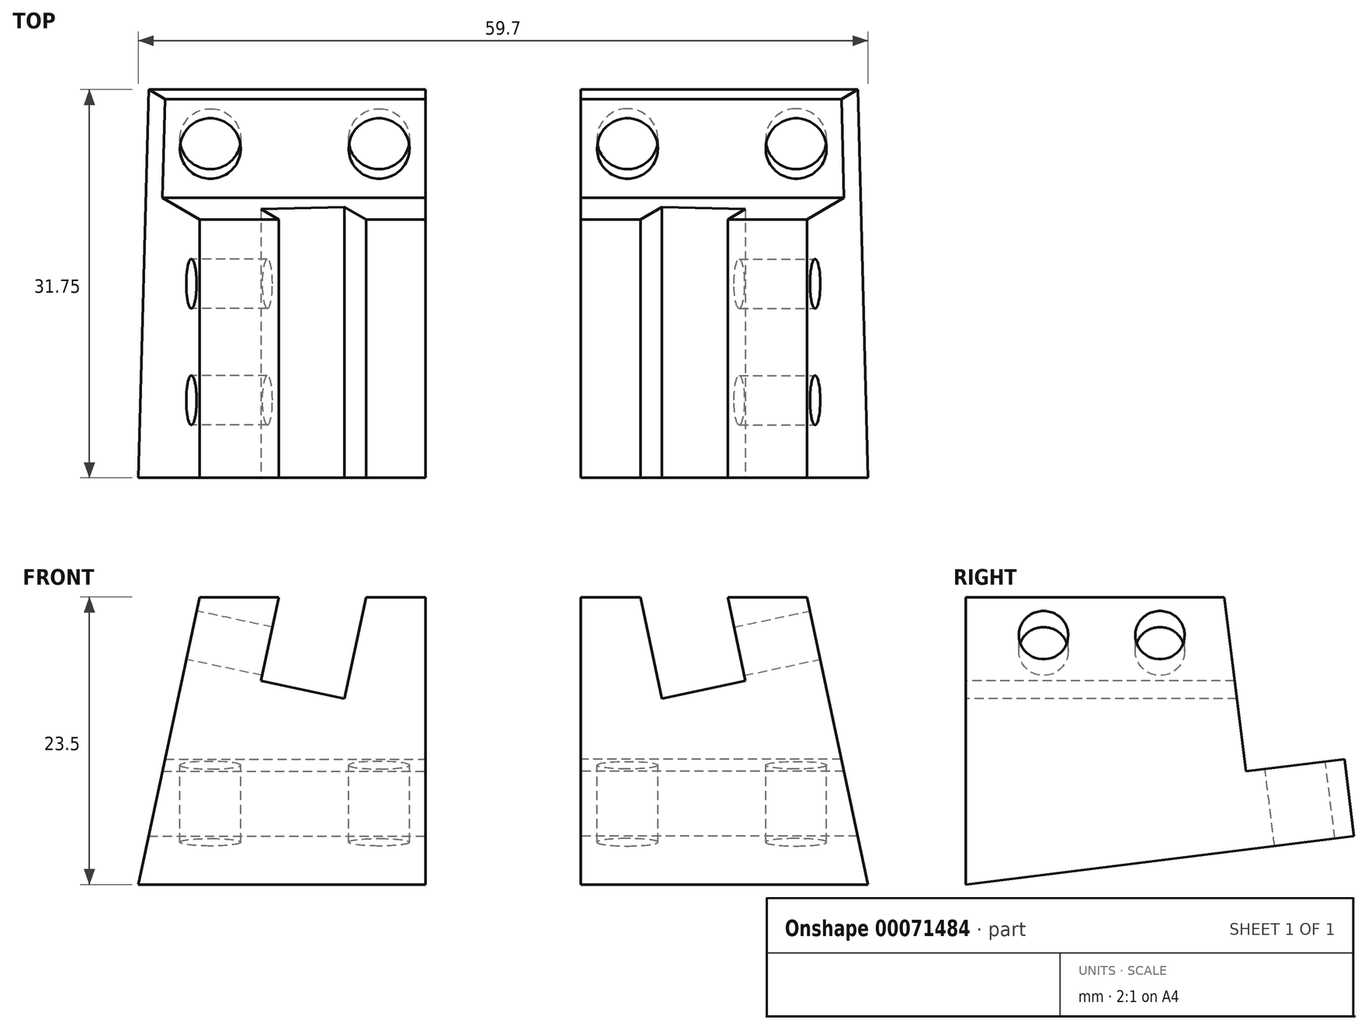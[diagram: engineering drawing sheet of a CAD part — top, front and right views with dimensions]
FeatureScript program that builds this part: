
annotation { "Feature Type Name" : "Feature", "Feature Type Description" : "" }
export const myFeature = defineFeature(function(context is Context, id is Id, definition is map)
    precondition{}
    {
        {
            var Q0;
            Q0=qCreatedBy(makeId("Front.planeOp"),FACE);
            var sketch = newSketch(context, id + "F0", { "sketchPlane" : qUnion([Q0])});
            skLineSegment(sketch, "E0.bottom", {"start": v(-29.85, 0) * mm, "end": v(-6.35, 0) * mm});
            skLineSegment(sketch, "E0.top", {"start": v(-29.85, 23.5) * mm, "end": v(-6.35, 23.5) * mm});
            skLineSegment(sketch, "E0.left", {"start": v(-29.85, 0) * mm, "end": v(-29.85, 23.5) * mm});
            skLineSegment(sketch, "E0.right", {"start": v(-6.35, 0) * mm, "end": v(-6.35, 23.5) * mm});
            skSolve(sketch);
        }
        {
            var Q0;
            Q0=makeQuery(id+"F0.imprint","IMPRINT",FACE,{"disambiguationData":[TD([[makeQuery(id+"F0.imprint","IMPRINT",EDGE,{"derivedFrom":sQuery(id+"F0.wireOp",EDGE,"E0.bottom")}),1.0]])]});
            extrude(context, id + "F1", {"entities" : qUnion([Q0]), "depth" : 31.75 * mm});
        }
        {
            var Q0;
            Q0=makeQuery(id+"F1.opExtrude","CAP_FACE",FACE,{"disambiguationData":[OSD([sQuery(id+"F0.wireOp",EDGE,"E0.bottom"),sQuery(id+"F0.wireOp",EDGE,"E0.top"),sQuery(id+"F0.wireOp",EDGE,"E0.left"),sQuery(id+"F0.wireOp",EDGE,"E0.right")])],"isStart":false});
            var sketch = newSketch(context, id + "F2", { "sketchPlane" : qUnion([Q0])});
            skLineSegment(sketch, "E1", {"start": v(-29.85, 0) * mm, "end": v(-24.85, 23.5) * mm});
            skLineSegment(sketch, "E2", {"start": v(-24.85, 23.5) * mm, "end": v(-29.85, 23.5) * mm});
            skLineSegment(sketch, "E3", {"start": v(-29.85, 23.5) * mm, "end": v(-29.85, 0) * mm});
            skSolve(sketch);
        }
        {
            var Q0;
            Q0 = qSketchRegion(id + "F2", true);
            extrude(context, id + "F3", {"entities" : qUnion([Q0]), "operationType" : NewBodyOperationType.REMOVE, "endBound" : BoundingType.THROUGH_ALL, "oppositeDirection" : true, "depth" : 25.4 * mm});
        }
        {
            var Q0;
            Q0=makeQuery(id+"F1.opExtrude","CAP_FACE",FACE,{"disambiguationData":[OSD([sQuery(id+"F0.wireOp",EDGE,"E0.bottom"),sQuery(id+"F0.wireOp",EDGE,"E0.top"),sQuery(id+"F0.wireOp",EDGE,"E0.left"),sQuery(id+"F0.wireOp",EDGE,"E0.right")])],"isStart":false});
            var sketch = newSketch(context, id + "F4", { "sketchPlane" : qUnion([Q0])});
            skLineSegment(sketch, "E4", {"start": v(-18.36, 23.5) * mm, "end": v(-19.81, 16.66) * mm});
            skLineSegment(sketch, "E5", {"start": v(-19.81, 16.66) * mm, "end": v(-12.98, 15.21) * mm});
            skLineSegment(sketch, "E6", {"start": v(-12.98, 15.21) * mm, "end": v(-11.22, 23.5) * mm});
            skLineSegment(sketch, "E7", {"start": v(-18.36, 23.5) * mm, "end": v(-11.22, 23.5) * mm});
            skSolve(sketch);
        }
        {
            var Q0;
            Q0 = qSketchRegion(id + "F4", true);
            extrude(context, id + "F5", {"entities" : qUnion([Q0]), "operationType" : NewBodyOperationType.REMOVE, "endBound" : BoundingType.THROUGH_ALL, "oppositeDirection" : true, "depth" : 25.4 * mm});
        }
        {
            var Q0;
            Q0=makeQuery(id+"F3.boolean.opBoolean","COPY",FACE,{"derivedFrom":makeQuery(id+"F3.opExtrude","SWEPT_FACE",FACE,{"disambiguationData":[OSD([sQuery(id+"F2.wireOp",EDGE,"E1")])]})});
            var sketch = newSketch(context, id + "F6", { "sketchPlane" : qUnion([Q0])});
            skLineSegment(sketch, "E8", {"start": v(25.4, 14.64) * mm, "end": v(31.75, 14.64) * mm, "construction": true});
            skPoint(sketch, "E9", {"position": v(25.4, 14.64) * mm});
            skPoint(sketch, "E10", {"position": v(15.88, 14.64) * mm});
            skSolve(sketch);
        }
        {
            var Q0;
            Q0=sQuery(id+"F6.wireOp",VERTEX,"E9");
            var Q1;
            Q1=sQuery(id+"F6.wireOp",VERTEX,"E10");
            var Q2;
            Q2=makeQuery(id+"F1.opExtrude","SWEPT_BODY",BODY,{"disambiguationData":[OSD([sQuery(id+"F0.wireOp",EDGE,"E0.bottom"),sQuery(id+"F0.wireOp",EDGE,"E0.top"),sQuery(id+"F0.wireOp",EDGE,"E0.left"),sQuery(id+"F0.wireOp",EDGE,"E0.right")])]});
            hole(context, id + "F7", {"style" : HoleStyle.SIMPLE, "holeDiameter" : 4.04 * mm, "endStyle" : HoleEndStyle.BLIND, "holeDepth" : 6.35 * mm, "locations" : qUnion([Q0, Q1]), "scope" : qUnion([Q2])});
        }
        {
            var Q0;
            Q0=makeQuery(id+"F1.opExtrude","SWEPT_FACE",FACE,{"disambiguationData":[OSD([sQuery(id+"F0.wireOp",EDGE,"E0.right")])]});
            var sketch = newSketch(context, id + "F8", { "sketchPlane" : qUnion([Q0])});
            skLineSegment(sketch, "E11", {"start": v(-31.75, 0) * mm, "end": v(0, 3.95) * mm});
            skLineSegment(sketch, "E12", {"start": v(0, 3.95) * mm, "end": v(0, 0) * mm});
            skLineSegment(sketch, "E13", {"start": v(0, 0) * mm, "end": v(-31.75, 0) * mm});
            skLineSegment(sketch, "E14", {"start": v(0, 10.35) * mm, "end": v(-8.85, 9.25) * mm});
            skLineSegment(sketch, "E15", {"start": v(-8.85, 9.25) * mm, "end": v(-10.62, 23.5) * mm});
            skLineSegment(sketch, "E16", {"start": v(-10.62, 23.5) * mm, "end": v(0, 23.5) * mm});
            skLineSegment(sketch, "E17", {"start": v(0, 23.5) * mm, "end": v(0, 10.35) * mm});
            skLineSegment(sketch, "E18", {"start": v(0, 3.95) * mm, "end": v(0, 10.35) * mm});
            skLineSegment(sketch, "E19", {"start": v(-0.78, 10.26) * mm, "end": v(0, 3.95) * mm});
            skSolve(sketch);
        }
        {
            var Q0;
            Q0 = qSketchRegion(id + "F8", true);
            extrude(context, id + "F9", {"entities" : qUnion([Q0]), "operationType" : NewBodyOperationType.REMOVE, "endBound" : BoundingType.THROUGH_ALL, "oppositeDirection" : true, "depth" : 25.4 * mm});
        }
        {
            var Q0;
            Q0=makeQuery(id+"F9.boolean.opBoolean","COPY",FACE,{"derivedFrom":makeQuery(id+"F9.opExtrude","SWEPT_FACE",FACE,{"disambiguationData":[OSD([sQuery(id+"F8.wireOp",EDGE,"E14")])]})});
            var sketch = newSketch(context, id + "F10", { "sketchPlane" : qUnion([Q0])});
            skPoint(sketch, "E20", {"position": v(-23.96, -3.58) * mm});
            skPoint(sketch, "E21", {"position": v(-10.16, -3.58) * mm});
            skLineSegment(sketch, "E22", {"start": v(-10.16, 0.49) * mm, "end": v(-10.16, -3.58) * mm, "construction": true});
            skLineSegment(sketch, "E23", {"start": v(-10.16, -7.64) * mm, "end": v(-10.16, -3.58) * mm, "construction": true});
            skLineSegment(sketch, "E24", {"start": v(-23.96, -3.58) * mm, "end": v(-23.96, 0.49) * mm, "construction": true});
            skLineSegment(sketch, "E25", {"start": v(-23.96, 0.49) * mm, "end": v(-23.96, -3.58) * mm, "construction": true});
            skLineSegment(sketch, "E26", {"start": v(-23.96, -7.64) * mm, "end": v(-23.96, -3.58) * mm, "construction": true});
            skLineSegment(sketch, "E27", {"start": v(-10.16, -3.58) * mm, "end": v(-6.35, -3.58) * mm, "construction": true});
            skLineSegment(sketch, "E28", {"start": v(-23.96, -3.58) * mm, "end": v(-27.77, -3.58) * mm, "construction": true});
            skSolve(sketch);
        }
        {
            var Q0;
            Q0=sQuery(id+"F10.wireOp",VERTEX,"E20");
            var Q1;
            Q1=sQuery(id+"F10.wireOp",VERTEX,"E21");
            var Q2;
            Q2=makeQuery(id+"F1.opExtrude","SWEPT_BODY",BODY,{"disambiguationData":[OSD([sQuery(id+"F0.wireOp",EDGE,"E0.bottom"),sQuery(id+"F0.wireOp",EDGE,"E0.top"),sQuery(id+"F0.wireOp",EDGE,"E0.left"),sQuery(id+"F0.wireOp",EDGE,"E0.right")])]});
            hole(context, id + "F11", {"style" : HoleStyle.SIMPLE, "holeDiameter" : 4.98 * mm, "endStyle" : HoleEndStyle.THROUGH, "locations" : qUnion([Q0, Q1]), "scope" : qUnion([Q2])});
        }
        {
            var Q0;
            Q0=makeQuery(id+"F1.opExtrude","SWEPT_BODY",BODY,{"disambiguationData":[OSD([sQuery(id+"F0.wireOp",EDGE,"E0.bottom"),sQuery(id+"F0.wireOp",EDGE,"E0.top"),sQuery(id+"F0.wireOp",EDGE,"E0.left"),sQuery(id+"F0.wireOp",EDGE,"E0.right")])]});
            var Q1;
            Q1=qCreatedBy(makeId("Right.planeOp"),FACE);
            mirror(context, id + "F12", {"entities" : qUnion([Q0]), "mirrorPlane" : qUnion([Q1])});
        }
    });
